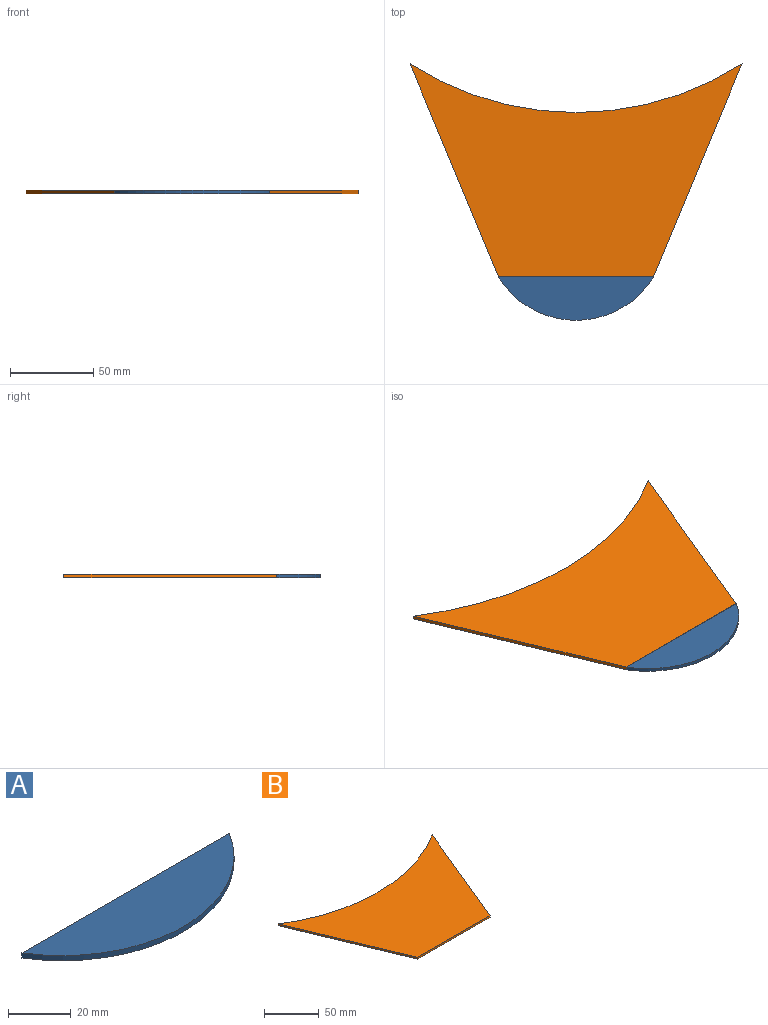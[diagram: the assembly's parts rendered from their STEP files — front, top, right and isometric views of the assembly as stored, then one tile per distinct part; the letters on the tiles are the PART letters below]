
ASSEMBLY  parts=2 mates=1
PART A: 4 faces, bbox 93.7x26.2x2 mm
  f0: plane 93.74x2mm, normal (0,1,0), area 187.5mm2, adj f1,f2,f3
  f1: cylinder r=55mm len=93.74mm, axis (0,0,1), area 224.4mm2, adj f0,f2,f3
  f2: plane 93.74x26.22mm, normal (0,0,1), area 1737.1mm2, adj f0,f1
  f3: plane 93.74x26.22mm, normal (0,0,-1), area 1737.1mm2, adj f0,f1
PART B: 6 faces, bbox 199.8x128.1x2 mm
  f0: cylinder r=185mm len=199.82mm, axis (0,0,1), area 422.2mm2, adj f1,f3,f4,f5
  f1: plane 128.07x53.22mm, normal (-0.92,-0.38,0), area 277.4mm2, adj f0,f2,f4,f5
  f2: plane 93.38x2mm, normal (0,-1,0), area 186.8mm2, adj f1,f3,f4,f5
  f3: plane 128.07x53.22mm, normal (0.92,-0.38,0), area 277.4mm2, adj f0,f2,f4,f5
  f4: plane 199.82x128.07mm, normal (0,0,1), area 14806.7mm2, adj f0,f1,f2,f3
  f5: plane 199.82x128.07mm, normal (0,0,-1), area 14806.7mm2, adj f0,f1,f2,f3
PLACE A t=(23.42,44.43,-129.74)mm
PLACE B t=(23.42,44.43,-129.74)mm
MATE fastened A.f2 <-> B.f4  axis (0,0,1) through (23.42,-34.35,25.26)mm
